FCSTD DOCUMENT  (FreeCAD 0.19R0.19.2)
Label: v0_06_mount positionLinesInPlace
License: All rights reserved
LicenseURL: http://en.wikipedia.org/wiki/All_rights_reserved
objects: Sketcher::SketchObject×1
note: 1 computed .brp shape members not serialized (recipe doc carries the construction recipe); baked Part::Feature solids carry a one-line shape summary decoded from their .brp

FEATURE [Sketcher::SketchObject] Sketch
  FullyConstrained = false
  sketch-geometry (32):
    g0: LineSegment StartX=0 StartY=0 StartZ=0 EndX=111.35 EndY=0 EndZ=0
    g1: Circle CenterX=111.35 CenterY=-15.15 CenterZ=0 NormalX=0 NormalY=0 NormalZ=1 AngleXU=0 Radius=3.25
    g2: LineSegment StartX=111.35 StartY=0 StartZ=0 EndX=144.4 EndY=0 EndZ=0
    g3: LineSegment StartX=144.9 StartY=-7.5 StartZ=0 EndX=151.9 EndY=-7.5 EndZ=0
    g4: LineSegment StartX=111.35 StartY=0 StartZ=0 EndX=98.1 EndY=0 EndZ=0
    g5: Circle CenterX=106.25 CenterY=37.0888 CenterZ=0 NormalX=0 NormalY=0 NormalZ=1 AngleXU=0 Radius=1.3
    g6: Circle CenterX=86.1497 CenterY=37.0888 CenterZ=0 NormalX=0 NormalY=0 NormalZ=1 AngleXU=0 Radius=1.3
    g7: LineSegment StartX=111.35 StartY=0 StartZ=0 EndX=81.35 EndY=0 EndZ=0
    g8: LineSegment StartX=144.4 StartY=0 StartZ=0 EndX=144.4 EndY=-7 EndZ=0
    g9: ArcOfCircle CenterX=144.9 CenterY=-7 CenterZ=0 NormalX=0 NormalY=0 NormalZ=1 AngleXU=0 Radius=0.5 StartAngle=3.14159 EndAngle=4.71239
    g10: Circle CenterX=106.25 CenterY=29.0888 CenterZ=0 NormalX=0 NormalY=0 NormalZ=1 AngleXU=0 Radius=1.3
    g11: Circle CenterX=86.1497 CenterY=29.0888 CenterZ=0 NormalX=0 NormalY=0 NormalZ=1 AngleXU=0 Radius=1.3
    g12: LineSegment StartX=151.9 StartY=-7.5 StartZ=0 EndX=151.9 EndY=-20.4 EndZ=0
    g13: LineSegment StartX=86.1497 StartY=29.0888 StartZ=0 EndX=106.25 EndY=29.0888 EndZ=0
    g14: LineSegment StartX=106.25 StartY=29.0888 StartZ=0 EndX=106.25 EndY=37.0888 EndZ=0
    g15: LineSegment StartX=86.1497 StartY=29.0888 StartZ=0 EndX=86.1497 EndY=37.0888 EndZ=0
    g16: LineSegment StartX=81.35 StartY=0 StartZ=0 EndX=81.35 EndY=-35.3 EndZ=0
    g17: LineSegment StartX=44.35 StartY=-35.3 StartZ=0 EndX=81.35 EndY=-35.3 EndZ=0
    g18: LineSegment StartX=81.35 StartY=-35.3 StartZ=0 EndX=151.9 EndY=-35.3 EndZ=0
    g19: LineSegment StartX=151.9 StartY=-20.4 StartZ=0 EndX=151.9 EndY=-35.3 EndZ=0
    g20: LineSegment StartX=44.35 StartY=2.2e-15 StartZ=0 EndX=44.35 EndY=-28 EndZ=0
    g21-g25: Circle x5 (B-spline internal-alignment scaffolding for g26; pole/knot coordinates omitted)
    g26: BSplineCurve PolesCount=5 KnotsCount=3 Degree=3 IsPeriodic=0
    g27: GeomPoint X=15.15 Y=-28 Z=0
    g28: GeomPoint X=29.75 Y=-31.65 Z=0
    g29: GeomPoint X=44.35 Y=-35.3 Z=0
    g30: LineSegment StartX=0 StartY=0 StartZ=0 EndX=0 EndY=-28 EndZ=0
    g31: LineSegment StartX=15.15 StartY=-28 StartZ=0 EndX=0 EndY=-28 EndZ=0
  constraints (64):
    c: Coincident(g0,g-1)
    c: PointOnObject(g0,g-1)
    c: Distance(g0) = 111.35
    c: Radius(g1) = 3.25
    c: Block(g1)
    c: Horizontal(g2)
    c: Distance(g2) = 33.05
    c: Coincident(g2,g0)
    c: Horizontal(g4)
    c: Distance(g4) = 13.25
    c: Coincident(g4,g0)
    c: Horizontal(g7)
    c: Distance(g7) = 30
    c: Coincident(g7,g0)
    c: Vertical(g8)
    c: Distance(g8) = 7
    c: Coincident(g8,g2)
    c: Coincident(g9,g8)
    c: Coincident(g9,g3)
    c: Block(g3)
    c: Block(g9)
    c: Vertical(g12)
    c: Coincident(g12,g3)
    c: Block(g12)
    c: Horizontal(g13)
    c: Vertical(g14)
    c: Vertical(g15)
    c: Coincident(g15,g6)
    c: Coincident(g15,g11)
    c: Coincident(g13,g11)
    c: Coincident(g13,g10)
    c: Coincident(g14,g10)
    c: Coincident(g5,g14)
    c: DistanceX(g13,g13) = 20.1
    c: DistanceY(g15,g15) = 8
    c: DistanceY(g14,g14) = 8
    c: Vertical(g16)
    c: Distance(g16) = 35.3
    c: Coincident(g16,g7)
    c: Horizontal(g17)
    c: Distance(g17) = 37
    c: Coincident(g17,g16)
    c: Horizontal(g18)
    c: Coincident(g18,g16)
    c: Vertical(g19)
    c: Coincident(g18,g19)
    c: Vertical(g20)
    c: Distance(g20) = 28
    c: Block(g20)
    c: Weight(g21) = 1
    c: Equal(g21, g22-g25) x4
    c: Coincident(g26,g17)
    c: InternalAlignment(g21-g25 -> g26) x5
    c: InternalAlignment(g27,g26)
    c: InternalAlignment(g28,g26)
    c: InternalAlignment(g29,g26)
    c: Vertical(g30)
    c: Coincident(g30,g0)
    c: Horizontal(g31)
    c: Coincident(g31,g30)
    c: Block(g26)
    c: Block(g18)
    c: Block(g19)
    c: Block(g31)
